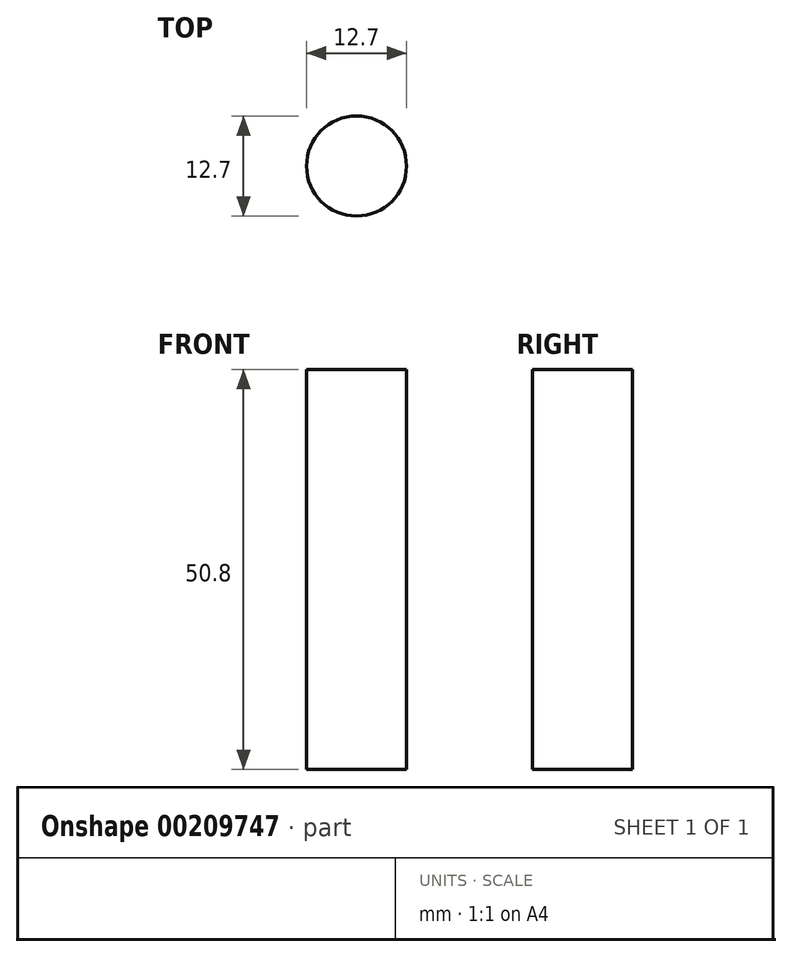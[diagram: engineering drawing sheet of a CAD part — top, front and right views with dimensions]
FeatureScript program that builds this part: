
annotation { "Feature Type Name" : "Feature", "Feature Type Description" : "" }
export const myFeature = defineFeature(function(context is Context, id is Id, definition is map)
    precondition{}
    {
        {
            var Q0;
            Q0=qCreatedBy(makeId("Front.planeOp"),FACE);
            var sketch = newSketch(context, id + "F0", { "sketchPlane" : qUnion([Q0])});
            skLineSegment(sketch, "E0.bottom", {"start": v(0, 0) * mm, "end": v(6.35, 0) * mm});
            skLineSegment(sketch, "E0.top", {"start": v(0, 50.8) * mm, "end": v(6.35, 50.8) * mm});
            skLineSegment(sketch, "E0.left", {"start": v(0, 0) * mm, "end": v(0, 50.8) * mm});
            skLineSegment(sketch, "E0.right", {"start": v(6.35, 0) * mm, "end": v(6.35, 50.8) * mm});
            skSolve(sketch);
        }
        {
            var Q0;
            Q0 = qSketchRegion(id + "F0", true);
            var Q1;
            Q1=sQuery(id+"F0.wireOp",EDGE,"E0.left");
            revolve(context, id + "F1", {"entities" : qUnion([Q0]), "axis" : qUnion([Q1]), "revolveType" : RevolveType.FULL});
        }
    });
